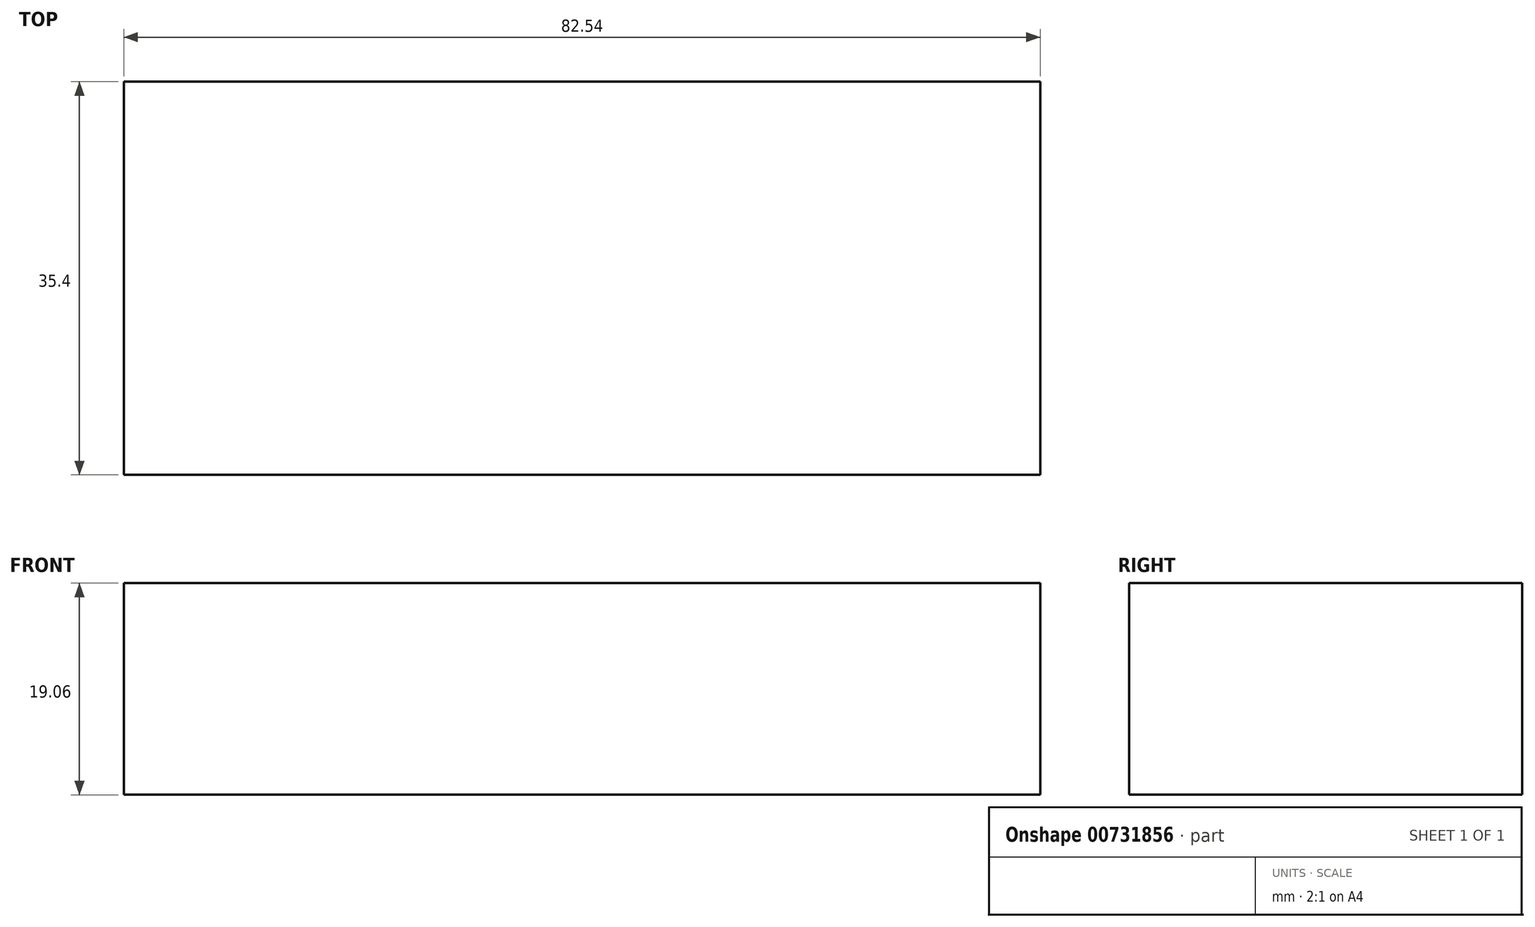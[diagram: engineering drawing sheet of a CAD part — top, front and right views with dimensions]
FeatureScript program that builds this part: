
annotation { "Feature Type Name" : "Feature", "Feature Type Description" : "" }
export const myFeature = defineFeature(function(context is Context, id is Id, definition is map)
    precondition{}
    {
        {
            var Q0;
            Q0=qCreatedBy(makeId("Front.planeOp"),FACE);
            var sketch = newSketch(context, id + "F0", { "sketchPlane" : qUnion([Q0])});
            skLineSegment(sketch, "E0.bottom", {"start": v(41.28, -9.52) * mm, "end": v(-41.28, -9.53) * mm});
            skLineSegment(sketch, "E0.top", {"start": v(41.28, 9.53) * mm, "end": v(-41.28, 9.53) * mm});
            skLineSegment(sketch, "E0.left", {"start": v(41.28, -9.52) * mm, "end": v(41.28, 9.53) * mm});
            skLineSegment(sketch, "E0.right", {"start": v(-41.28, -9.53) * mm, "end": v(-41.28, 9.53) * mm});
            skPoint(sketch, "E0.middle", {"position": v(0, 0) * mm});
            skLineSegment(sketch, "E1", {"start": v(41.28, 9.53) * mm, "end": v(41.28, 42.59) * mm});
            skArc(sketch, "E2", {"start": v(41.27, 42.59) * mm, "mid": v(45.92, 53.81) * mm, "end": v(57.15, 58.46) * mm});
            skLineSegment(sketch, "E3.bottom", {"start": v(104.43, 39.14) * mm, "end": v(53.63, 39.14) * mm});
            skLineSegment(sketch, "E3.top", {"start": v(104.43, 67.71) * mm, "end": v(53.63, 67.71) * mm});
            skLineSegment(sketch, "E3.left", {"start": v(104.43, 39.14) * mm, "end": v(104.43, 67.71) * mm});
            skLineSegment(sketch, "E3.right", {"start": v(53.63, 39.14) * mm, "end": v(53.63, 67.71) * mm});
            skPoint(sketch, "E3.middle", {"position": v(79.03, 53.42) * mm});
            skLineSegment(sketch, "E4", {"start": v(57.15, 58.46) * mm, "end": v(79.03, 58.46) * mm});
            skPoint(sketch, "E4.endSnap0", {"position": v(79.03, 67.71) * mm});
            skSolve(sketch);
        }
        {
            var Q0;
            Q0=makeQuery(id+"F0.imprint","IMPRINT",FACE,{"disambiguationData":[TD([[makeQuery(id+"F0.imprint","IMPRINT",EDGE,{"derivedFrom":sQuery(id+"F0.wireOp",EDGE,"E0.bottom")}),-1.0]])]});
            extrude(context, id + "F1", {"entities" : qUnion([Q0]), "depth" : 10 * mm, "offsetDistance" : 25.4 * mm, "hasSecondDirection" : true, "secondDirectionOppositeDirection" : true, "secondDirectionDepth" : 25.4 * mm});
        }
    });
